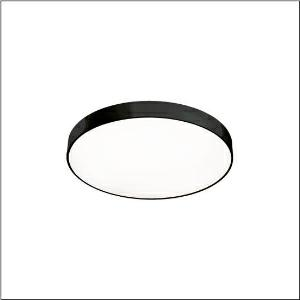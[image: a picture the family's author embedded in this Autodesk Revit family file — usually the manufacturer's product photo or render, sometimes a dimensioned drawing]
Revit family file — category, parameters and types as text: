
# Revit family: round_21_m_51mr36gd0421b
name_source: partatom
category: Lighting Fixtures
units: mm (PartAtom-declared; Revit-internal decimal feet)

## family parameters
Cut with Voids When Loaded = No
Host = Face
Light Source = No
Part Type = Normal
Room Calculation Point = No
Round Connector Dimension = Use Diameter
Shared = No

## types (1)
- Round 21 M (1 x LED, 7160 lm, 54.5 W, 4000K)
    Apparent Load = 55 VA
    CIE Flux Codes = 49 80 96 85 100
    Color Rendering = 80
    Color Temperature = 4000K
    Default Elevation = 1800 mm
    Description = Round 21 M, wall and ceiling luminaire, primary optical cover: cover, of PMMA, opal, light emission: direct/indirect distribution, primary light characteristic: symmetric, installation type: suspended mounting, surface-mounted, LED, rated luminous flux: 7.110lm, luminous efficacy: 130lm/W, light colour: 840, colour temperature: 4000K, with terminal, 5-pole, mains connection: 230V, AC, 50/60Hz, rated input power: 55W, housing, of aluminium, coated, black, diameter: 600mm, height: 62mm, protection rating (complete): IP40, insulation class (complete): insulation class I (protective earthing), certification: CE, impact resistance: IK04, permissible operating ambient temperature: -10..+35°C, packaging unit: 1 piece
    Height = 87 mm
    Lamp = 1 x LED
    Lamp Light Flux = 7160 lm
    Lamp Power = 54.5 W
    Lamp count = 1
    Length = 600 mm
    Luminous efficacy = 131 lm/W
    Manufacturer = Siteco
    ModVariant = No
    Model = 51MR36GD0421B
    Mounting Place = Ceiling
    Mounting Type = Surface mounted
    Number of Poles = 1
    OnlyDefault = Yes
    Power Factor = 1
    Product Name = Round 21 M
    Product group = wall and ceiling luminaire
    ProductGroupID = 302
    Protection Class = Protection class I
    Protection Degree = IP 40
    RLX_Detail_Level = 1
    RLX_Emergency_Light_Flux = 0 lm
    RLX_Emergency_Type = 0
    RLX_Emergency_Type_DB = No
    RlxData = <blob elided: 18101 chars, md5=2ed4e20f>
    Socket = socket
    Standby Power = 0 W
    System Light Flux = 7160 lm
    System Power = 55 W
    Type Comments = Product without accessories
    Type Image = l_1258332.jpg
    URL = http://relux.com
    VarID = ---
    Voltage = 0 V
    Weight = 0.00 kg
    Width = 0 mm  [stored 0 ft]

note: [stored X ft] marks values corroborated as IEEE doubles in the binary element streams (Revit-internal decimal feet)

## geometry (parser evidence)
native form markers: Blend x4, Sweep x11
no freeform markers — native parametric forms only
